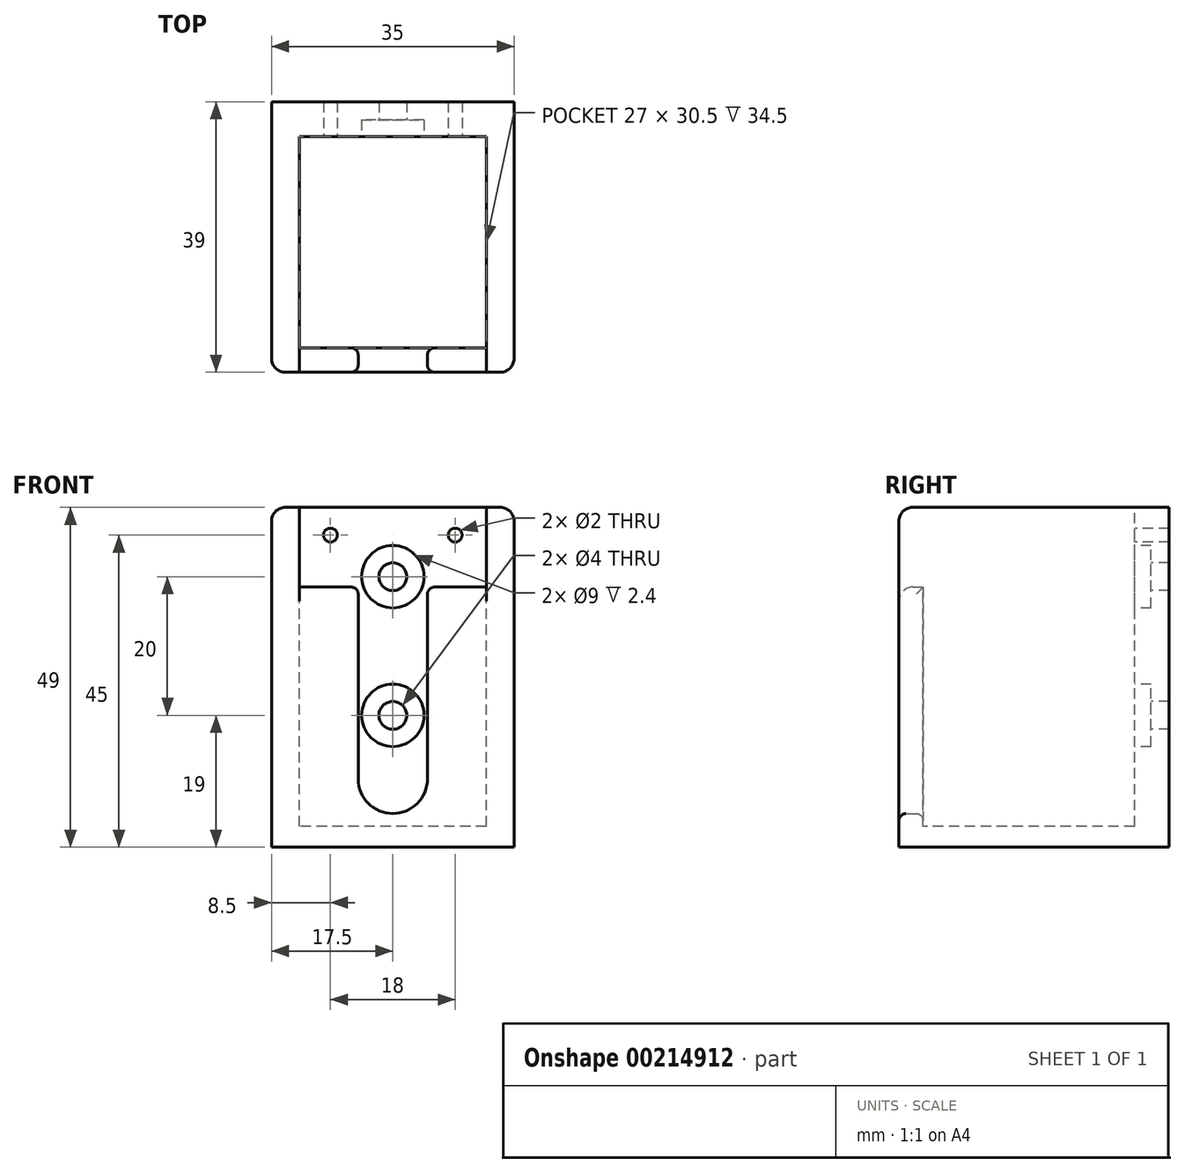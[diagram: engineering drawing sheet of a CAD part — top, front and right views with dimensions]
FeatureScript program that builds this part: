
annotation { "Feature Type Name" : "Feature", "Feature Type Description" : "" }
export const myFeature = defineFeature(function(context is Context, id is Id, definition is map)
    precondition{}
    {
        {
            var Q0;
            Q0=qCreatedBy(makeId("Front.planeOp"),FACE);
            var sketch = newSketch(context, id + "F0", { "sketchPlane" : qUnion([Q0])});
            skLineSegment(sketch, "E0", {"start": v(0, 0) * mm, "end": v(-13.5, 0) * mm});
            skLineSegment(sketch, "E1", {"start": v(-13.5, 0) * mm, "end": v(-13.5, 72) * mm});
            skLineSegment(sketch, "E2", {"start": v(-13.5, 72) * mm, "end": v(0, 72) * mm});
            skLineSegment(sketch, "E3", {"start": v(0, 0) * mm, "end": v(0, 42) * mm});
            skLineSegment(sketch, "E4", {"start": v(0, 42) * mm, "end": v(-9, 42) * mm});
            skLineSegment(sketch, "E5.MirrorCS", {"start": v(0, 42) * mm, "end": v(9, 42) * mm});
            skLineSegment(sketch, "E6.MirrorCS", {"start": v(13.5, 0) * mm, "end": v(13.5, 72) * mm});
            skLineSegment(sketch, "E7.MirrorCS", {"start": v(13.5, 72) * mm, "end": v(0, 72) * mm});
            skLineSegment(sketch, "E8.MirrorCS", {"start": v(0, 0) * mm, "end": v(13.5, 0) * mm});
            skLineSegment(sketch, "E9", {"start": v(-13.5, 36) * mm, "end": v(-13.5, 46) * mm});
            skLineSegment(sketch, "E10", {"start": v(-13.5, 46) * mm, "end": v(-17.5, 46) * mm});
            skLineSegment(sketch, "E11", {"start": v(-17.5, 46) * mm, "end": v(-17.5, 0) * mm});
            skLineSegment(sketch, "E12", {"start": v(-17.5, 0) * mm, "end": v(-17.5, -3) * mm});
            skLineSegment(sketch, "E13", {"start": v(-17.5, -3) * mm, "end": v(13.5, -3) * mm});
            skLineSegment(sketch, "E14", {"start": v(13.5, -3) * mm, "end": v(13.5, 0) * mm});
            skLineSegment(sketch, "E15.MirrorCS", {"start": v(13.5, 46) * mm, "end": v(17.5, 46) * mm});
            skLineSegment(sketch, "E16.MirrorCS", {"start": v(17.5, 46) * mm, "end": v(17.5, 0) * mm});
            skLineSegment(sketch, "E17.MirrorCS", {"start": v(17.5, 0) * mm, "end": v(17.5, -3) * mm});
            skLineSegment(sketch, "E18.MirrorCS", {"start": v(17.5, -3) * mm, "end": v(-13.5, -3) * mm});
            skLineSegment(sketch, "E19", {"start": v(-13.5, 46) * mm, "end": v(13.5, 46) * mm});
            skLineSegment(sketch, "E20", {"start": v(-9, 42) * mm, "end": v(-9, 34.5) * mm});
            skLineSegment(sketch, "E21", {"start": v(-9, 34.5) * mm, "end": v(13.5, 34.5) * mm});
            skLineSegment(sketch, "E22", {"start": v(13.5, 34.5) * mm, "end": v(-13.5, 34.5) * mm});
            skSolve(sketch);
        }
        {
            var Q0;
            {var subQ2=sQuery(id+"F0.wireOp",EDGE,"E0");Q0=makeQuery(id+"F0.imprint","IMPRINT",FACE,{"disambiguationData":[TD([[makeQuery(id+"F0.imprint","IMPRINT",EDGE,{"derivedFrom":subQ2}),1.0]])]});}
            var Q1;
            {var subQ1=sQuery(id+"F0.wireOp",EDGE,"E14");Q1=makeQuery(id+"F0.imprint","IMPRINT",FACE,{"disambiguationData":[TD([[makeQuery(id+"F0.imprint","IMPRINT",EDGE,{"derivedFrom":subQ1}),-1.0]])]});}
            var Q2;
            {var subQ4=sQuery(id+"F0.wireOp",EDGE,"E0");Q2=makeQuery(id+"F0.imprint","IMPRINT",FACE,{"disambiguationData":[TD([[makeQuery(id+"F0.imprint","IMPRINT",EDGE,{"derivedFrom":subQ4}),-1.0]])]});}
            var Q3;
            {var subQ7=sQuery(id+"F0.wireOp",EDGE,"E4");Q3=makeQuery(id+"F0.imprint","IMPRINT",FACE,{"disambiguationData":[TD([[makeQuery(id+"F0.imprint","IMPRINT",EDGE,{"derivedFrom":subQ7}),-1.0]])]});}
            var Q4;
            {var subQ0=sQuery(id+"F0.wireOp",EDGE,"E4");Q4=makeQuery(id+"F0.imprint","IMPRINT",FACE,{"disambiguationData":[TD([[makeQuery(id+"F0.imprint","IMPRINT",EDGE,{"derivedFrom":subQ0}),1.0]])]});}
            var Q5;
            {var subQ0=sQuery(id+"F0.wireOp",EDGE,"E8.MirrorCS");Q5=makeQuery(id+"F0.imprint","IMPRINT",FACE,{"disambiguationData":[TD([[makeQuery(id+"F0.imprint","IMPRINT",EDGE,{"derivedFrom":subQ0}),1.0]])]});}
            extrude(context, id + "F1", {"entities" : qUnion([Q0, Q1, Q2, Q3, Q4, Q5]), "oppositeDirection" : true, "depth" : 39 * mm});
        }
        {
            var Q0;
            {var subQ4=sQuery(id+"F0.wireOp",EDGE,"E0");Q0=makeQuery(id+"F0.imprint","IMPRINT",FACE,{"disambiguationData":[TD([[makeQuery(id+"F0.imprint","IMPRINT",EDGE,{"derivedFrom":subQ4}),-1.0]])]});}
            var Q1;
            {var subQ0=sQuery(id+"F0.wireOp",EDGE,"E8.MirrorCS");Q1=makeQuery(id+"F0.imprint","IMPRINT",FACE,{"disambiguationData":[TD([[makeQuery(id+"F0.imprint","IMPRINT",EDGE,{"derivedFrom":subQ0}),1.0]])]});}
            var Q2;
            {var subQ7=sQuery(id+"F0.wireOp",EDGE,"E4");Q2=makeQuery(id+"F0.imprint","IMPRINT",FACE,{"disambiguationData":[TD([[makeQuery(id+"F0.imprint","IMPRINT",EDGE,{"derivedFrom":subQ7}),-1.0]])]});}
            var Q3;
            {var subQ0=sQuery(id+"F0.wireOp",EDGE,"E4");Q3=makeQuery(id+"F0.imprint","IMPRINT",FACE,{"disambiguationData":[TD([[makeQuery(id+"F0.imprint","IMPRINT",EDGE,{"derivedFrom":subQ0}),1.0]])]});}
            extrude(context, id + "F2", {"entities" : qUnion([Q0, Q1, Q2, Q3]), "operationType" : NewBodyOperationType.REMOVE, "oppositeDirection" : true, "depth" : 34 * mm});
        }
        {
            var Q0;
            Q0=sQuery(id+"F0.wireOp",VERTEX,"E4.end");
            var Q1;
            Q1=sQuery(id+"F0.wireOp",VERTEX,"E5.MirrorCS.end");
            var Q2;
            Q2=makeQuery(id+"F1.opExtrude","SWEPT_BODY",BODY,{"disambiguationData":[OSD([sQuery(id+"F0.wireOp",EDGE,"E10"),sQuery(id+"F0.wireOp",EDGE,"E11"),sQuery(id+"F0.wireOp",EDGE,"E12"),sQuery(id+"F0.wireOp",EDGE,"E13"),sQuery(id+"F0.wireOp",EDGE,"E15.MirrorCS"),sQuery(id+"F0.wireOp",EDGE,"E16.MirrorCS"),sQuery(id+"F0.wireOp",EDGE,"E17.MirrorCS"),sQuery(id+"F0.wireOp",EDGE,"E18.MirrorCS"),sQuery(id+"F0.wireOp",EDGE,"E19")])]});
            hole(context, id + "F3", {"style" : HoleStyle.SIMPLE, "endStyle" : HoleEndStyle.BLIND, "holeDiameter" : 2 * mm, "holeDepth" : 40 * mm, "locations" : qUnion([Q0, Q1]), "scope" : qUnion([Q2])});
        }
        {
            var Q0;
            {var subQ4=sQuery(id+"F0.wireOp",EDGE,"E0");Q0=makeQuery(id+"F0.imprint","IMPRINT",FACE,{"disambiguationData":[TD([[makeQuery(id+"F0.imprint","IMPRINT",EDGE,{"derivedFrom":subQ4}),-1.0]])]});}
            var Q1;
            {var subQ0=sQuery(id+"F0.wireOp",EDGE,"E8.MirrorCS");Q1=makeQuery(id+"F0.imprint","IMPRINT",FACE,{"disambiguationData":[TD([[makeQuery(id+"F0.imprint","IMPRINT",EDGE,{"derivedFrom":subQ0}),1.0]])]});}
            extrude(context, id + "F4", {"entities" : qUnion([Q0, Q1]), "operationType" : NewBodyOperationType.ADD, "oppositeDirection" : true, "depth" : 3.5 * mm});
        }
        {
            var Q0;
            {var subQ0=sQuery(id+"F0.wireOp",EDGE,"E19");var subQ1=sQuery(id+"F0.wireOp",EDGE,"E15.MirrorCS");var subQ2=sQuery(id+"F0.wireOp",EDGE,"E12");var subQ3=sQuery(id+"F0.wireOp",EDGE,"E11");var subQ4=sQuery(id+"F0.wireOp",EDGE,"E10");Q0=makeQuery(id+"F2.boolean.opBoolean","SPLIT",EDGE,{"disambiguationData":[TD([makeQuery(id+"F1.opExtrude","SWEPT_FACE",FACE,{"disambiguationData":[OSD([subQ3,subQ2])]})])],"derivedFrom":makeQuery(id+"F1.opExtrude","CAP_EDGE",EDGE,{"disambiguationData":[OSD([subQ4,subQ1,subQ0])],"isStart":true})});}
            var Q1;
            Q1=makeQuery(id+"F1.opExtrude","CAP_EDGE",EDGE,{"disambiguationData":[OSD([sQuery(id+"F0.wireOp",EDGE,"E11"),sQuery(id+"F0.wireOp",EDGE,"E12")])],"isStart":true});
            var Q2;
            Q2=makeQuery(id+"F1.opExtrude","CAP_EDGE",EDGE,{"disambiguationData":[OSD([sQuery(id+"F0.wireOp",EDGE,"E16.MirrorCS"),sQuery(id+"F0.wireOp",EDGE,"E17.MirrorCS")])],"isStart":true});
            var Q3;
            {var subQ0=sQuery(id+"F0.wireOp",EDGE,"E19");var subQ3=sQuery(id+"F0.wireOp",EDGE,"E15.MirrorCS");var subQ4=sQuery(id+"F0.wireOp",EDGE,"E10");Q3=makeQuery(id+"F2.boolean.opBoolean","SPLIT",EDGE,{"disambiguationData":[TD([makeQuery(id+"F2.opExtrude","SWEPT_FACE",FACE,{"disambiguationData":[OSD([sQuery(id+"F0.wireOp",EDGE,"E6.MirrorCS")])]})])],"derivedFrom":makeQuery(id+"F1.opExtrude","CAP_EDGE",EDGE,{"disambiguationData":[OSD([subQ4,subQ3,subQ0])],"isStart":true})});}
            var Q4;
            Q4=makeQuery(id+"F1.opExtrude","SWEPT_EDGE",EDGE,{"disambiguationData":[OSD([sQuery(id+"F0.wireOp",EDGE,"E10"),sQuery(id+"F0.wireOp",EDGE,"E11")])]});
            var Q5;
            Q5=makeQuery(id+"F1.opExtrude","SWEPT_EDGE",EDGE,{"disambiguationData":[OSD([sQuery(id+"F0.wireOp",EDGE,"E15.MirrorCS"),sQuery(id+"F0.wireOp",EDGE,"E16.MirrorCS")])]});
            var Q6;
            Q6=makeQuery(id+"F2.boolean.opBoolean","COPY",EDGE,{"derivedFrom":makeQuery(id+"F2.opExtrude","CAP_EDGE",EDGE,{"disambiguationData":[OSD([sQuery(id+"F0.wireOp",EDGE,"E19")])],"isStart":false})});
            var Q7;
            Q7=makeQuery(id+"F2.boolean.opBoolean","COPY",EDGE,{"derivedFrom":makeQuery(id+"F2.opExtrude","SWEPT_EDGE",EDGE,{"disambiguationData":[OSD([sQuery(id+"F0.wireOp",EDGE,"E6.MirrorCS"),sQuery(id+"F0.wireOp",EDGE,"E15.MirrorCS"),sQuery(id+"F0.wireOp",EDGE,"E19")])]})});
            var Q8;
            Q8=makeQuery(id+"F2.boolean.opBoolean","COPY",EDGE,{"derivedFrom":makeQuery(id+"F2.opExtrude","SWEPT_EDGE",EDGE,{"disambiguationData":[OSD([sQuery(id+"F0.wireOp",EDGE,"E1"),sQuery(id+"F0.wireOp",EDGE,"E9"),sQuery(id+"F0.wireOp",EDGE,"E10"),sQuery(id+"F0.wireOp",EDGE,"E19")])]})});
            var Q9;
            Q9=makeQuery(id+"F4.opExtrude","CAP_EDGE",EDGE,{"disambiguationData":[OSD([sQuery(id+"F0.wireOp",EDGE,"E22")])],"isStart":true});
            fillet(context, id + "F5", {"entities" : qUnion([Q0, Q1, Q2, Q3, Q4, Q5, Q6, Q7, Q8, Q9]), "radius" : 2 * mm, "tangentPropagation" : true, "allowEdgeOverflow" : false});
        }
        {
            var Q0;
            Q0=makeQuery(id+"F2.boolean.opBoolean","COPY",FACE,{"derivedFrom":makeQuery(id+"F2.opExtrude","CAP_FACE",FACE,{"disambiguationData":[OSD([sQuery(id+"F0.wireOp",EDGE,"E0"),sQuery(id+"F0.wireOp",EDGE,"E1"),sQuery(id+"F0.wireOp",EDGE,"E6.MirrorCS"),sQuery(id+"F0.wireOp",EDGE,"E8.MirrorCS"),sQuery(id+"F0.wireOp",EDGE,"E9"),sQuery(id+"F0.wireOp",EDGE,"E19")])],"isStart":false})});
            var sketch = newSketch(context, id + "F6", { "sketchPlane" : qUnion([Q0])});
            skLineSegment(sketch, "E23", {"start": v(0, 0) * mm, "end": v(0, 16) * mm});
            skLineSegment(sketch, "E24", {"start": v(0, 16) * mm, "end": v(0, 36) * mm});
            skCircle(sketch, "E25", {"center": v(0, 6.83) * mm, "radius": 5 * mm});
            skLineSegment(sketch, "E26", {"start": v(0, 6.83) * mm, "end": v(-5, 6.83) * mm});
            skLineSegment(sketch, "E27", {"start": v(-5, 6.83) * mm, "end": v(-5, 35.08) * mm});
            skLineSegment(sketch, "E28", {"start": v(-5, 35.08) * mm, "end": v(5, 35.08) * mm});
            skLineSegment(sketch, "E29", {"start": v(5, 35.08) * mm, "end": v(5, 6.83) * mm});
            skSolve(sketch);
        }
        {
            var Q0;
            Q0=sQuery(id+"F6.wireOp",VERTEX,"E24.end");
            var Q1;
            Q1=sQuery(id+"F6.wireOp",VERTEX,"E24.start");
            var Q2;
            Q2=makeQuery(id+"F1.opExtrude","SWEPT_BODY",BODY,{"disambiguationData":[OSD([sQuery(id+"F0.wireOp",EDGE,"E10"),sQuery(id+"F0.wireOp",EDGE,"E11"),sQuery(id+"F0.wireOp",EDGE,"E12"),sQuery(id+"F0.wireOp",EDGE,"E13"),sQuery(id+"F0.wireOp",EDGE,"E15.MirrorCS"),sQuery(id+"F0.wireOp",EDGE,"E16.MirrorCS"),sQuery(id+"F0.wireOp",EDGE,"E17.MirrorCS"),sQuery(id+"F0.wireOp",EDGE,"E18.MirrorCS"),sQuery(id+"F0.wireOp",EDGE,"E19")])]});
            hole(context, id + "F7", {"style" : HoleStyle.C_BORE, "endStyle" : HoleEndStyle.BLIND, "holeDiameter" : 4 * mm, "cBoreDiameter" : 9 * mm, "cBoreDepth" : 2.4 * mm, "holeDepth" : 10 * mm, "locations" : qUnion([Q0, Q1]), "scope" : qUnion([Q2])});
        }
        {
            var Q0;
            Q0 = qSketchRegion(id + "F6", true);
            extrude(context, id + "F8", {"entities" : qUnion([Q0]), "operationType" : NewBodyOperationType.REMOVE, "depth" : 50 * mm});
        }
        {
            var Q0;
            Q0=makeQuery(id+"F8.boolean.opBoolean","INTERSECT",EDGE,{"derivedFrom":[makeQuery(id+"F4.opExtrude","CAP_FACE",FACE,{"disambiguationData":[OSD([sQuery(id+"F0.wireOp",EDGE,"E0"),sQuery(id+"F0.wireOp",EDGE,"E1"),sQuery(id+"F0.wireOp",EDGE,"E6.MirrorCS"),sQuery(id+"F0.wireOp",EDGE,"E8.MirrorCS"),sQuery(id+"F0.wireOp",EDGE,"E22")])],"isStart":false}),makeQuery(id+"F8.opExtrude","SWEPT_FACE",FACE,{"disambiguationData":[OSD([sQuery(id+"F6.wireOp",EDGE,"E29")])]})]});
            var Q1;
            Q1=makeQuery(id+"F8.boolean.opBoolean","INTERSECT",EDGE,{"derivedFrom":[makeQuery(id+"F4.boolean.opBoolean","MERGE",FACE,{"derivedFrom":[makeQuery(id+"F1.opExtrude","CAP_FACE",FACE,{"disambiguationData":[OSD([sQuery(id+"F0.wireOp",EDGE,"E10"),sQuery(id+"F0.wireOp",EDGE,"E11"),sQuery(id+"F0.wireOp",EDGE,"E12"),sQuery(id+"F0.wireOp",EDGE,"E13"),sQuery(id+"F0.wireOp",EDGE,"E15.MirrorCS"),sQuery(id+"F0.wireOp",EDGE,"E16.MirrorCS"),sQuery(id+"F0.wireOp",EDGE,"E17.MirrorCS"),sQuery(id+"F0.wireOp",EDGE,"E18.MirrorCS"),sQuery(id+"F0.wireOp",EDGE,"E19")])],"isStart":true}),makeQuery(id+"F4.opExtrude","CAP_FACE",FACE,{"disambiguationData":[OSD([sQuery(id+"F0.wireOp",EDGE,"E0"),sQuery(id+"F0.wireOp",EDGE,"E1"),sQuery(id+"F0.wireOp",EDGE,"E6.MirrorCS"),sQuery(id+"F0.wireOp",EDGE,"E8.MirrorCS"),sQuery(id+"F0.wireOp",EDGE,"E22")])],"isStart":true})]}),makeQuery(id+"F8.opExtrude","SWEPT_FACE",FACE,{"disambiguationData":[OSD([sQuery(id+"F6.wireOp",EDGE,"E29")])]})]});
            var Q2;
            Q2=makeQuery(id+"F8.boolean.opBoolean","INTERSECT",EDGE,{"derivedFrom":[makeQuery(id+"F4.opExtrude","CAP_FACE",FACE,{"disambiguationData":[OSD([sQuery(id+"F0.wireOp",EDGE,"E0"),sQuery(id+"F0.wireOp",EDGE,"E1"),sQuery(id+"F0.wireOp",EDGE,"E6.MirrorCS"),sQuery(id+"F0.wireOp",EDGE,"E8.MirrorCS"),sQuery(id+"F0.wireOp",EDGE,"E22")])],"isStart":false}),makeQuery(id+"F8.opExtrude","SWEPT_FACE",FACE,{"disambiguationData":[OSD([sQuery(id+"F6.wireOp",EDGE,"E25")])]})]});
            fillet(context, id + "F9", {"entities" : qUnion([Q0, Q1, Q2]), "radius" : 1 * mm, "tangentPropagation" : true, "allowEdgeOverflow" : false});
        }
    });
